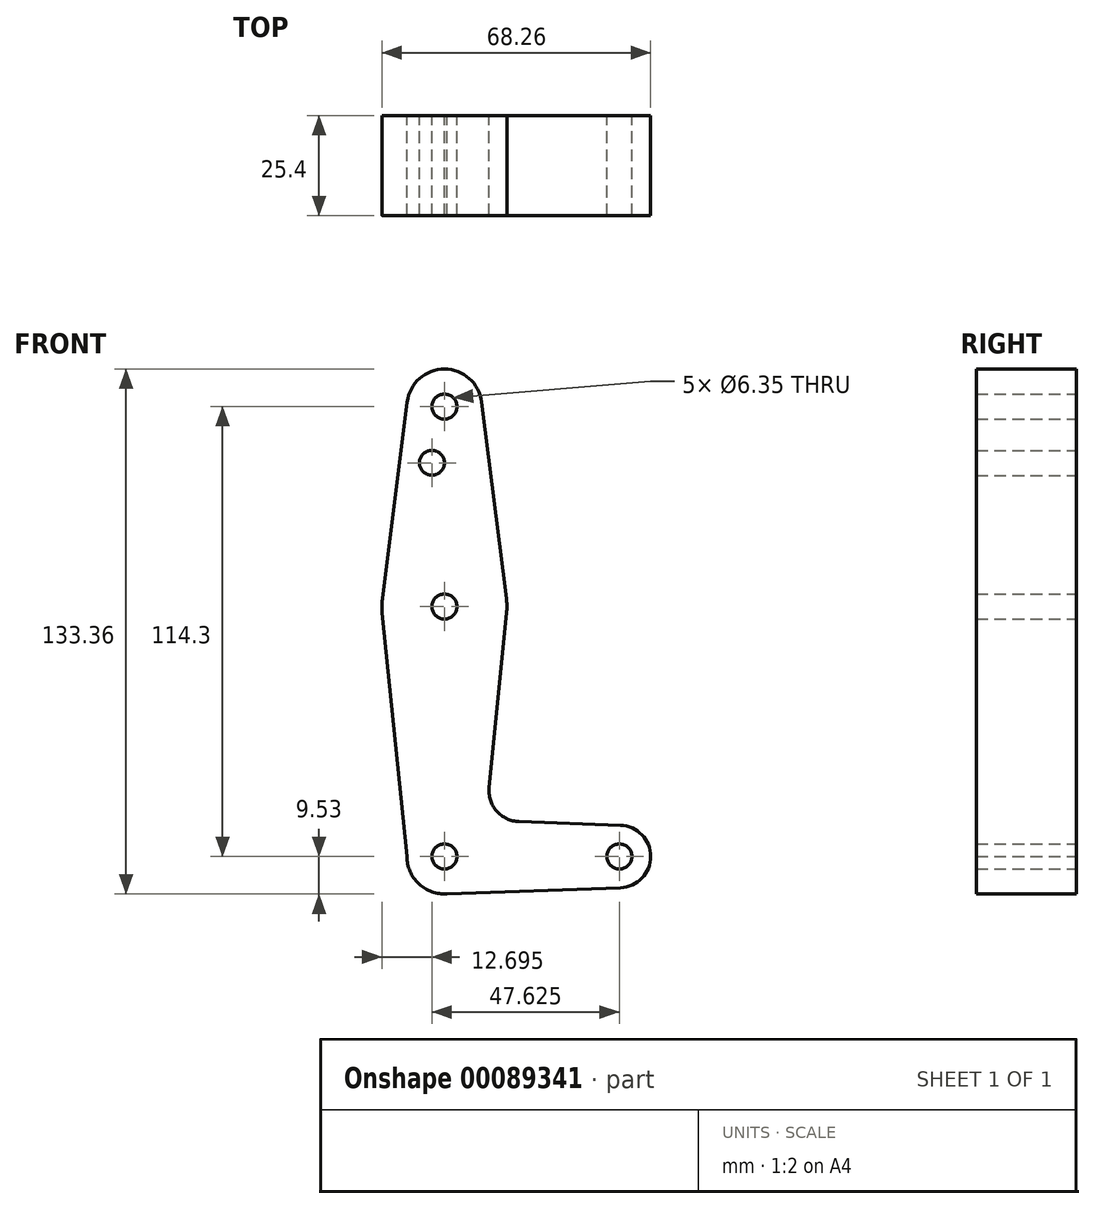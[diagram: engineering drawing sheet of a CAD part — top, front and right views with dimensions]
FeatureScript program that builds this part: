
annotation { "Feature Type Name" : "Feature", "Feature Type Description" : "" }
export const myFeature = defineFeature(function(context is Context, id is Id, definition is map)
    precondition{}
    {
        {
            var Q0;
            Q0=qCreatedBy(makeId("Front.planeOp"),FACE);
            var sketch = newSketch(context, id + "F0", { "sketchPlane" : qUnion([Q0])});
            skSolve(sketch);
        }
        {
            var Q0;
            Q0=qCreatedBy(makeId("Front.planeOp"),FACE);
            var sketch = newSketch(context, id + "F1", { "sketchPlane" : qUnion([Q0])});
            skSolve(sketch);
        }
        {
            var Q0;
            Q0=qCreatedBy(makeId("Front.planeOp"),FACE);
            var sketch = newSketch(context, id + "F2", { "sketchPlane" : qUnion([Q0])});
            skCircle(sketch, "E0", {"center": v(0, 63.5) * mm, "radius": 15.88 * mm});
            skCircle(sketch, "E1", {"center": v(0, 0) * mm, "radius": 9.53 * mm});
            skCircle(sketch, "E2", {"center": v(44.45, 0) * mm, "radius": 7.94 * mm});
            skCircle(sketch, "E3", {"center": v(0, 114.3) * mm, "radius": 9.53 * mm});
            skLineSegment(sketch, "E4", {"start": v(0, -9.52) * mm, "end": v(44.73, -7.93) * mm});
            skCircle(sketch, "E5", {"center": v(44.45, 0) * mm, "radius": 3.18 * mm});
            skCircle(sketch, "E6", {"center": v(0, 0) * mm, "radius": 3.18 * mm});
            skCircle(sketch, "E7", {"center": v(0, 63.5) * mm, "radius": 3.18 * mm});
            skCircle(sketch, "E8", {"center": v(0, 114.3) * mm, "radius": 3.18 * mm});
            skCircle(sketch, "E9", {"center": v(-3.18, 100.03) * mm, "radius": 3.18 * mm});
            skLineSegment(sketch, "E10", {"start": v(15.8, 61.91) * mm, "end": v(11.34, 17.59) * mm});
            skLineSegment(sketch, "E11", {"start": v(18.97, 8.85) * mm, "end": v(44.73, 7.93) * mm});
            skPoint(sketch, "E12.newPointA", {"position": v(9.57, 0) * mm});
            skPoint(sketch, "E12.newPointB", {"position": v(0, 9.53) * mm});
            skArc(sketch, "E12.filletArc", {"start": v(11.34, 17.59) * mm, "mid": v(13.26, 11.57) * mm, "end": v(18.97, 8.85) * mm});
            skLineSegment(sketch, "E13", {"start": v(0, 114.3) * mm, "end": v(0, 0) * mm, "construction": true});
            skLineSegment(sketch, "E14", {"start": v(-9.45, 115.5) * mm, "end": v(-15.75, 65.48) * mm});
            skLineSegment(sketch, "E15", {"start": v(9.45, 115.5) * mm, "end": v(15.8, 65.13) * mm});
            skLineSegment(sketch, "E16", {"start": v(-9.53, 0) * mm, "end": v(-15.8, 61.9) * mm});
            skSolve(sketch);
        }
        {
            var Q0;
            Q0 = qSketchRegion(id + "FDGtC1iRoDHmR7h_0", true);
            var Q1;
            Q1 = qSketchRegion(id + "F2", true);
            var Q2;
            Q2 = qSketchRegion(id + "F1", true);
            var Q3;
            Q3 = qSketchRegion(id + "F4CbVo6YRUk1l4O_0", true);
            var Q4;
            Q4 = qSketchRegion(id + "F0", true);
            var Q5;
            Q5 = qSketchRegion(id + "FDwEpiit8Sjp9QN_0", true);
            extrude(context, id + "F3", {"entities" : qUnion([Q0, Q1, Q2, Q3, Q4, Q5]), "depth" : 25.4 * mm});
        }
    });
